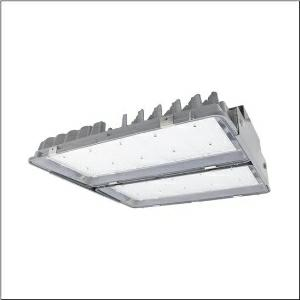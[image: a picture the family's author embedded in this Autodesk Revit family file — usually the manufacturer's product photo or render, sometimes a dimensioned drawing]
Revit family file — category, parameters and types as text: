
# Revit family: highbay_11xtreme_51hf62db4qma
name_source: partatom
category: Lighting Fixtures
units: mm (PartAtom-declared; Revit-internal decimal feet)

## family parameters
Cut with Voids When Loaded = No
Host = Face
Light Source = No
Part Type = Normal
Room Calculation Point = No
Round Connector Dimension = Use Diameter
Shared = No

## types (1)
- --- (1 x LED, 36800 lm, 193.7 W, 4000K)
    Apparent Load = 194 VA
    CIE Flux Codes = 84 96 100 100 100
    Color Rendering = 80
    Color Temperature = 4000K
    Default Elevation = 1800 mm
    Description = Highbay 11Xtreme, high bay luminaire, primary light control with lens, of PMMA, primary optical cover: cover, of toughened safety glass, light emission: direct distribution, primary light characteristic: symmetric, installation type: suspended mounting, surface-mounted, 2x LED module,for 1x 2x LED, rated luminous flux: 36.000lm, luminous efficacy: 178lm/W, light colour: 840, colour temperature: 4000K, control gear: DALI 2 (with two DALI addresses), with cable H07RN-F 5x 1.5mm², mains connection: 220..240V, AC, 50/60Hz, cable length: 1,5m, rated input power: 202W, luminaire housing, of diecast aluminium, coated, silver, length: 595mm, width: 560mm, height: 195mm, protection rating (complete): IP66, insulation class (complete): insulation class I (protective earthing), certification: CE, ENEC, UKCA, protection symbol: D, ball protection: ball impact resistant according to DIN VDE 0710 part 13 (with chain suspension), impact resistance: IK08, permissible operating ambient temperature: -25..+70°C, reducing of maximum allowable ambient temperature of 5°C with ceiling mounting, packaging unit: 1 piece
    Height = 157 mm
    Lamp = 1 x LED
    Lamp Light Flux = 36800 lm
    Lamp Power = 193.7 W
    Lamp count = 1
    Length = 593 mm
    Luminous efficacy = 190 lm/W
    Manufacturer = Siteco
    ModVariant = No
    Model = 51HF62DB4QMA
    Mounting Place = Ceiling
    Mounting Type = Pendant
    Number of Poles = 1
    OnlyDefault = Yes
    Power Factor = 1
    Product Name = Highbay 11Xtreme
    Product group = high bay luminaire
    ProductGroupID = 901
    Protection Class = Protection class I
    Protection Degree = IP 66
    RLX_Detail_Level = 1
    RLX_Emergency_Light_Flux = 0 lm
    RLX_Emergency_Type = 0
    RLX_Emergency_Type_DB = No
    RlxData = <blob elided: 34337 chars, md5=d847da8f>
    Socket = socket
    Standby Power = 0 W
    System Light Flux = 36799 lm
    System Power = 194 W
    Type Comments = factory setting: luminous flux: 100 % | dim-lin: 254 | 648 mA
    Type Image = l_1258340.jpg
    URL = http://relux.com
    VarID = @adj_083278
    Voltage = 0 V
    Weight = 0.00 kg
    Width = 568 mm

## geometry (parser evidence)
native form markers: Blend x4, Sweep x10
no freeform markers — native parametric forms only
